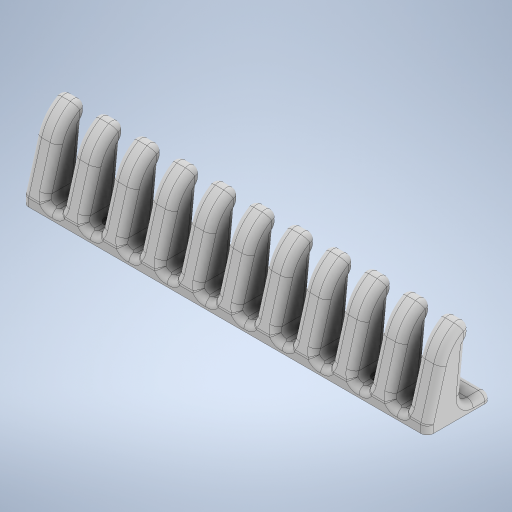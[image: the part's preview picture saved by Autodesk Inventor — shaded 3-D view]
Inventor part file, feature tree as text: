
AUTODESK INVENTOR PART (.ipt)
format: ipt  version: 2023 (Build 270158030, 158C)  size: 1,215,488 bytes
history: native  units: mm
features: fillet x10, sketch x4, extrude x3, hole x1
ambient origin geometry x8: Origin, YZ Plane, XZ Plane, XY Plane, X Axis, Y Axis, Z Axis, Center Point
bodies: Solid1 (feature_tree)
feature tree (18):
  extrude  "Extrusion1"  Depth=190.0mm
  extrude  "Extrusion2"  Depth=4.0mm
  extrude  "Extrusion3"  Depth=10.0mm
  fillet  "Fillet1"  Radius=190.0mm
  fillet  "Fillet3"  Radius=35.0mm
  fillet  "Fillet6"  Radius=10.0mm
  fillet  "Fillet10"  Radius=16.0mm
  fillet  "Fillet11"  [1 undecoded]
  fillet  "Fillet12"  Radius=5.0mm
  fillet  "Fillet13"  Radius=20.0mm
  fillet  "Fillet14"  Radius=3.0mm
  fillet  "Fillet15"  Radius=3.0mm
  fillet  "Fillet16"  Radius=3.0mm
  hole  "Hole1"  [1 undecoded]
  sketch  "Sketch1"  dims[d0=30.0mm d1=190.0mm]
  sketch  "Sketch2"  dims[d2=4.0mm d3=0.0mm d4=20.0mm]
  sketch  "Sketch3"  dims[d5=10.0mm d18=110.0mm d20=18.0mm d21=10.0mm d23=10.0mm d25=190.0mm d26=35.0mm d27=0.0mm d28=10.0mm d29=16.0mm d30=0.0mm d31=0.0mm d32=5.0mm d34=20.0mm d37=3.0mm d41=3.0mm d42=3.0mm]
  sketch  "Sketch4"  dims[d43=3.0mm d44=3.0mm d45=3.0mm d46=3.0mm d47=3.0mm d48=3.0mm d49=9.0mm d50=4.0mm d51=4.0mm d52=4.0mm d53=4.0mm d54=24.2mm d55=3.242mm d56=8.0mm d57=5.0mm d58=1.0mm d59=90.0deg d60=8.0mm d61=20.594885mm d62=29.0mm d63=30.0mm d64=1.0mm d65=0.0mm d66=0.0mm d67=0.0mm d68=0.0mm]
note: 2 required parameter values undecoded (feature->parameter linkage not recoverable at this tier; creation-order binding heuristic only, values carry confidence <= 0.55)
